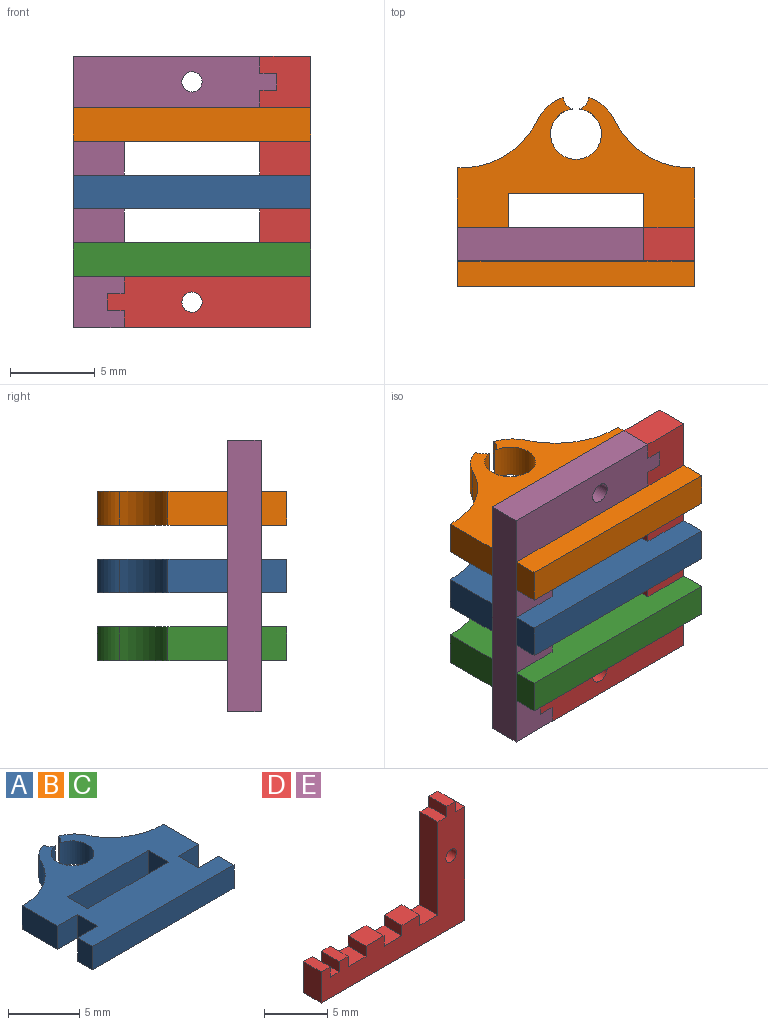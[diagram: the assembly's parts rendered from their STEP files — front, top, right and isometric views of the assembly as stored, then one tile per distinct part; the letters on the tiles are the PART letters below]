
ASSEMBLY  parts=5 mates=11
PART A: 26 faces, bbox 14x11.2x2 mm
  f0: cylinder r=2.5mm len=2mm, axis (0,0,-1), area 4.1mm2, adj f3,f5,f6,f25
  f1: cylinder r=0.75mm len=2mm, axis (0,0,-1), area 1.8mm2, adj f2,f4,f5,f6
  f2: cylinder r=2.5mm len=2mm, axis (0,0,-1), area 4.1mm2, adj f1,f5,f6,f24
  f3: cylinder r=0.75mm len=2mm, axis (0,0,-1), area 1.8mm2, adj f0,f4,f5,f6
  f4: cylinder r=1.5mm len=3mm, axis (0,0,-1), area 18mm2, adj f1,f3,f5,f6
  f5: plane 14x11.17mm, normal (0,0,1), area 90.8mm2, adj f0,f1,f2,f3,f4,f7,f8,f9
  f6: plane 14x11.17mm, normal (0,0,-1), area 90.8mm2, adj f0,f1,f2,f3,f4,f7,f8,f9
  f7: plane 2x2mm, normal (1,0,0), area 4mm2, adj f5,f6,f8,f23
  f8: plane 8x2mm, normal (0,-1,0), area 16mm2, adj f5,f6,f7,f9
  f9: plane 2x2mm, normal (-1,0,0), area 4mm2, adj f5,f6,f8,f23
  f10: plane 2x0.23mm, normal (0,1,0), area 0.5mm2, adj f5,f6,f11,f24
  f11: plane 3.5x2mm, normal (-1,0,0), area 7mm2, adj f5,f6,f10,f12
  f12: plane 2x2mm, normal (0,-1,0), area 4mm2, adj f5,f6,f11,f13
  f13: plane 2x2mm, normal (-1,0,0), area 4mm2, adj f5,f6,f12,f14
  f14: plane 2x2mm, normal (0,1,0), area 4mm2, adj f5,f6,f13,f15
  f15: plane 2x1.5mm, normal (-1,0,0), area 3mm2, adj f5,f6,f14,f16
  f16: plane 14x2mm, normal (0,-1,0), area 28mm2, adj f5,f6,f15,f17
  f17: plane 2x1.5mm, normal (1,0,0), area 3mm2, adj f5,f6,f16,f18
  f18: plane 2x2mm, normal (0,1,0), area 4mm2, adj f5,f6,f17,f19
  f19: plane 2x2mm, normal (1,0,0), area 4mm2, adj f5,f6,f18,f20
  f20: plane 2x2mm, normal (0,-1,0), area 4mm2, adj f5,f6,f19,f21
  f21: plane 3.5x2mm, normal (1,0,0), area 7mm2, adj f5,f6,f20,f22
  f22: plane 2x0.23mm, normal (0,1,0), area 0.5mm2, adj f5,f6,f21,f25
  f23: plane 8x2mm, normal (0,1,0), area 16mm2, adj f5,f6,f7,f9
  f24: cylinder r=5mm len=4.52mm, axis (0,0,-1), area 11.3mm2, adj f2,f5,f6,f10
  f25: cylinder r=5mm len=4.52mm, axis (0,0,-1), area 11.3mm2, adj f0,f5,f6,f22
PART B: same geometry as A
PART C: same geometry as A
PART D: 27 faces, bbox 16x2x12 mm
  f0: plane 11x2mm, normal (1,0,0), area 22mm2, adj f1,f23,f25,f26
  f1: plane 2x1mm, normal (0,0,1), area 2mm2, adj f0,f2,f25,f26
  f2: plane 2x1mm, normal (1,0,0), area 2mm2, adj f1,f3,f25,f26
  f3: plane 2x1mm, normal (0,0,1), area 2mm2, adj f2,f4,f25,f26
  f4: plane 2x1mm, normal (-1,0,0), area 2mm2, adj f3,f5,f25,f26
  f5: plane 2x1mm, normal (0,0,1), area 2mm2, adj f4,f6,f25,f26
  f6: plane 9x2mm, normal (-1,0,0), area 18mm2, adj f5,f7,f25,f26
  f7: plane 2x2mm, normal (0,0,1), area 4mm2, adj f6,f8,f25,f26
  f8: plane 2x1mm, normal (1,0,0), area 2mm2, adj f7,f9,f25,f26
  f9: plane 2x2mm, normal (0,0,1), area 4mm2, adj f8,f10,f25,f26
  f10: plane 2x1mm, normal (-1,0,0), area 2mm2, adj f9,f11,f25,f26
  f11: plane 2x2mm, normal (0,0,1), area 4mm2, adj f10,f12,f25,f26
  f12: plane 2x1mm, normal (1,0,0), area 2mm2, adj f11,f13,f25,f26
  f13: plane 2x2mm, normal (0,0,1), area 4mm2, adj f12,f14,f25,f26
  f14: plane 2x1mm, normal (-1,0,0), area 2mm2, adj f13,f15,f25,f26
  f15: plane 2x2mm, normal (0,0,1), area 4mm2, adj f14,f16,f25,f26
  f16: plane 2x1mm, normal (1,0,0), area 2mm2, adj f15,f17,f25,f26
  f17: plane 2x1mm, normal (0,0,1), area 2mm2, adj f16,f18,f25,f26
  f18: plane 2x1mm, normal (-1,0,0), area 2mm2, adj f17,f19,f25,f26
  f19: plane 2x1mm, normal (0,0,1), area 2mm2, adj f18,f20,f25,f26
  f20: plane 2x1mm, normal (1,0,0), area 2mm2, adj f19,f21,f25,f26
  f21: plane 2x1mm, normal (0,0,1), area 2mm2, adj f20,f22,f25,f26
  f22: plane 3x2mm, normal (-1,0,0), area 6mm2, adj f21,f23,f25,f26
  f23: plane 16x2mm, normal (0,0,-1), area 32mm2, adj f0,f22,f25,f26
  f24: cylinder r=0.6mm len=2mm, axis (0,1,0), area 7.5mm2, adj f25,f26
  f25: plane 16x12mm, normal (0,-1,0), area 64.9mm2, adj f0,f1,f2,f3,f4,f5,f6,f7
  f26: plane 16x12mm, normal (0,1,0), area 64.9mm2, adj f0,f1,f2,f3,f4,f5,f6,f7
PART E: same geometry as D
PLACE A t=(-10.28,2.08,6.02)mm
PLACE B t=(-10.28,2.08,10.02)mm
PLACE C t=(-10.28,2.08,2.02)mm
PLACE D rot(axis=(0.71,0,-0.71),180deg) t=(-4.28,-5.42,7.02)mm
PLACE E rot(axis=(0.71,0,0.71),180deg) t=(-16.28,-5.42,7.02)mm
MATE planar E.f25 <-> B.f12  axis (0,1,0) through (-13.8,-3.42,9.52)mm
MATE planar D.f6 <-> C.f6  axis (0,0,1) through (-9.78,-4.42,2.02)mm
MATE planar A.f19 <-> D.f11  axis (1,0,0) through (-5.28,-4.42,7.02)mm
MATE planar B.f22 <-> C.f22  axis (0,1,0) through (-3.4,0.08,11.02)mm
MATE planar A.f22 <-> B.f22  axis (0,1,0) through (-3.4,0.08,7.02)mm
MATE planar D.f15 <-> C.f19  axis (-1,0,0) through (-5.28,-4.42,11.02)mm
MATE planar B.f19 <-> D.f15  axis (1,0,0) through (-5.28,-4.42,11.02)mm
MATE planar B.f5 <-> D.f16  axis (0,0,1) through (-10.28,-1.42,12.02)mm
MATE planar E.f25 <-> D.f25  axis (0,1,0) through (-11.78,-3.42,15.02)mm
MATE planar E.f7 <-> C.f13  axis (1,0,0) through (-15.28,-4.42,11.02)mm
MATE planar E.f0 <-> D.f22  axis (0,0,1) through (-11.78,-4.42,15.02)mm
